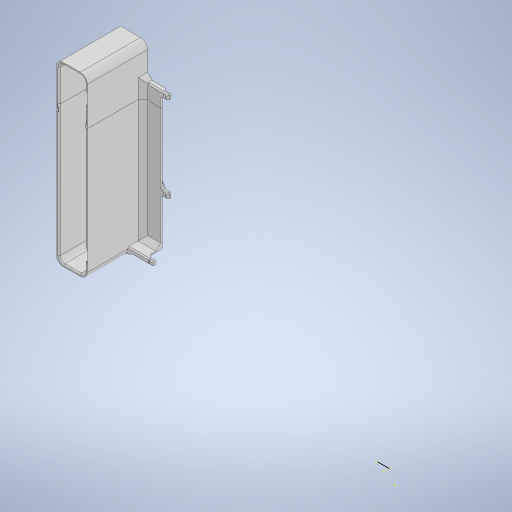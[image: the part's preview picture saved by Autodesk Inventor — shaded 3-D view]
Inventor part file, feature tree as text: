
AUTODESK INVENTOR PART (.ipt)
format: ipt  version: 2024.1 (Build 281209000, 209)  size: 7,091,200 bytes
history: native  units: mm
features: projected_geometry x112, sketch x91, extrude x86, chamfer x77, other x33, plane x15, fillet x9, pattern_linear x7, mirror x3, loft x2, pattern_circular x1, sweep x1
ambient origin geometry x8: Origin, YZ Plane, XZ Plane, XY Plane, X Axis, Y Axis, Z Axis, Center Point
bodies: Solid3 (feature_tree), Solid4 (feature_tree), Solid8 (feature_tree), Solid9 (feature_tree), Solid14 (feature_tree), Solid16 (feature_tree), Solid26 (feature_tree), Solid27 (feature_tree)
feature tree (437):
  other  "synth-a"
  other  "Blocks"
  extrude  "Extrusion1"  Depth=30.22mm
  plane  "Work Plane1"
  extrude  "Extrusion2"  Depth=17.13mm
  plane  "Work Plane2"
  mirror  "Mirror1"
  sketch  "Sketch3"  dims[d5=2.61mm d6=226.0mm]
  extrude  "Extrusion3"  Depth=226.0mm
  extrude  "Extrusion4"  Depth=8.2mm
  extrude  "Extrusion5"  Depth=35.4mm
  fillet  "Fillet1"  Radius=7.89mm
  pattern_linear  "Rectangular Pattern1"  Count1=56 Spacing1=0.0mm
  extrude  "Extrusion6"  Depth=3.14mm
  chamfer  "Chamfer1"  Distance=13.85mm
  chamfer  "Chamfer2"  Distance=440.5mm
  chamfer  "Chamfer3"  Distance=11.2mm
  chamfer  "Chamfer4"  Distance=3.1mm
  chamfer  "Chamfer5"  Distance=220.0mm
  chamfer  "Chamfer6"  Distance=7.26mm
  chamfer  "Chamfer7"  Distance=7.0mm Angle=45.0deg
  chamfer  "Chamfer8"  Distance=7.0mm Angle=45.0deg
  chamfer  "Chamfer9"  Distance=7.0mm Angle=45.0deg
  chamfer  "Chamfer10"  Distance=7.0mm Angle=45.0deg
  chamfer  "Chamfer11"  Distance=7.0mm Angle=45.0deg
  chamfer  "Chamfer12"  Distance=7.0mm Angle=45.0deg
  chamfer  "Chamfer13"  Distance=7.0mm Angle=45.0deg
  chamfer  "Chamfer14"  Distance=7.0mm Angle=45.0deg
  chamfer  "Chamfer15"  Distance=7.0mm Angle=45.0deg
  fillet  "Fillet2"  Radius=1.5mm
  pattern_linear  "Rectangular Pattern2"  Count1=3  [1 undecoded]
  extrude  "Extrusion7"  Depth=40.0mm
  extrude  "Extrusion8"  Depth=40.0mm
  plane  "Work Plane3"
  extrude  "Extrusion9"  Depth=20.42mm TaperAngle=0.0deg
  plane  "Work Plane7"
  plane  "Work Plane9"
  extrude  "Extrusion18"  Depth=60.6mm
  sketch  "Sketch26"  dims[d46=3.63mm]
  extrude  "Extrusion24"  Depth=35.8mm
  extrude  "Extrusion25"  Depth=2.9mm TaperAngle=0.0deg
  fillet  "Fillet3"  [1 undecoded]
  extrude  "Extrusion10"  Depth=90.0mm
  sketch  "Sketch12"  dims[d25=18.04mm]
  plane  "Work Plane5"
  extrude  "Extrusion12"  Depth=10.0mm
  extrude  "Extrusion14"  Depth=5.0mm
  extrude  "Extrusion15"  Depth=5.0mm
  plane  "Work Plane6"
  extrude  "Extrusion16"  Depth=16.580628mm
  mirror  "Mirror2"
  extrude  "Extrusion77"  Depth=20.0mm
  extrude  "Extrusion78"  Depth=5.0mm
  extrude  "Extrusion79"  Depth=2.0mm
  extrude  "Extrusion80"  Depth=2.5mm
  extrude  "Extrusion81"  Depth=2.5mm
  extrude  "Extrusion82"  Depth=2.5mm
  pattern_linear  "Rectangular Pattern4"  Count1=3 Spacing1=241.0mm
  chamfer  "Chamfer64"  Distance=10.0mm
  chamfer  "Chamfer65"  Distance=0.01mm
  chamfer  "Chamfer66"  Distance=10.0mm
  pattern_linear  "Rectangular Pattern3"  Count1=2 Spacing1=105.0mm
  pattern_linear  "Rectangular Pattern10"  Count1=2 Spacing1=0.0mm
  extrude  "Extrusion17"  Depth=2.0mm
  extrude  "Extrusion56"  Depth=4.0mm
  extrude  "Extrusion57"  Depth=3.0mm
  plane  "Work Plane8"
  plane  "Work Plane11"
  extrude  "Extrusion33"  Depth=4.0mm
  fillet  "Fillet6"  Radius=1.0mm
  extrude  "Extrusion29"  Depth=2.0mm
  extrude  "Extrusion31"  Depth=10.0mm
  extrude  "Extrusion32"  Depth=292.1mm
  extrude  "Extrusion34"  Depth=8.0mm
  extrude  "Extrusion35"  Depth=0.5mm TaperAngle=0.0deg
  extrude  "Extrusion36"  Depth=28.3mm
  fillet  "Fillet7"  Radius=28.3mm
  pattern_circular  "Circular Pattern1"  Count=7  [1 undecoded]
  extrude  "Extrusion37"  Depth=11.3mm
  plane  "Work Plane17"
  extrude  "Extrusion38"  Depth=13.54mm
  extrude  "Extrusion39"  Depth=2.0mm
  extrude  "Extrusion40"  Depth=2.0mm
  extrude  "Extrusion41"  Depth=2.0mm
  extrude  "Extrusion43"  Depth=2.0mm
  extrude  "Extrusion44"  Depth=2.0mm
  sketch  "Sketch47"  dims[d121=20.0mm d122=0.0mm d123=5.0mm]
  chamfer  "Chamfer18"  Distance=15.4mm
  chamfer  "Chamfer19"  Distance=2.0mm Angle=45.0deg
  chamfer  "Chamfer20"  Distance=2.0mm
  extrude  "Extrusion45"  Depth=2.0mm
  chamfer  "Chamfer21"  Distance=13.0mm
  extrude  "Extrusion46"  Depth=2.0mm
  extrude  "Extrusion49"  Depth=2.0mm TaperAngle=0.0deg
  extrude  "Extrusion50"  Depth=2.0mm
  plane  "Work Plane13"
  extrude  "Extrusion51"  Depth=2.0mm TaperAngle=0.0deg
  pattern_linear  "Rectangular Pattern7"  Spacing1=10.0mm  [1 undecoded]
  extrude  "Extrusion52"  Depth=4.0mm
  extrude  "Extrusion53"  Depth=2.0mm TaperAngle=0.0deg
  extrude  "Extrusion54"  Depth=2.0mm
  extrude  "Extrusion55"  Depth=2.0mm TaperAngle=0.0deg
  chamfer  "Chamfer22"  Distance=2.0mm Angle=45.0deg
  chamfer  "Chamfer23"  Distance=2.0mm
  chamfer  "Chamfer24"  Distance=150.0mm
  chamfer  "Chamfer25"  Distance=0.02mm
  extrude  "Extrusion74"  Depth=2.0mm TaperAngle=0.0deg
  chamfer  "Chamfer58"  Distance=14.55mm
  chamfer  "Chamfer59"  Distance=7.0mm
  plane  "Work Plane16"
  extrude  "Extrusion73"  Depth=2.0mm
  plane  "Work Plane14"
  extrude  "Extrusion75"  Depth=2.0mm
  chamfer  "Chamfer60"  Distance=2.5mm
  plane  "Work Plane15"
  extrude  "Extrusion71"  Depth=2.0mm
  extrude  "Extrusion72"  Depth=2.0mm TaperAngle=0.0deg
  chamfer  "Chamfer61"  Distance=17.0mm
  chamfer  "Chamfer62"  Distance=7.0mm
  extrude  "Extrusion83"  Depth=2.0mm
  extrude  "Extrusion84"  Depth=241.0mm
  extrude  "Extrusion85"  Depth=2.0mm
  extrude  "Extrusion86"  Depth=2.0mm
  extrude  "Extrusion87"  TaperAngle=90.0deg  [1 undecoded]
  loft  "Loft2"
  chamfer  "Chamfer68"  Angle=90.0deg  [1 undecoded]
  chamfer  "Chamfer69"  Distance=420.0mm
  chamfer  "Chamfer70"  Distance=7.0mm
  chamfer  "Chamfer71"  Distance=40.0mm
  chamfer  "Chamfer72"  Distance=7.0mm
  chamfer  "Chamfer73"  Distance=10.0mm
  chamfer  "Chamfer79"  Distance=4.2mm
  chamfer  "Chamfer80"  [1 undecoded]
  chamfer  "Chamfer81"  Distance=2.5mm
  chamfer  "Chamfer82"  Distance=8.0mm
  chamfer  "Chamfer83"  Distance=10.0mm
  sketch  "Sketch109"  dims[d216=16.2mm d217=28.3mm d218=28.3mm]
  extrude  "Extrusion91"  Depth=2.0mm TaperAngle=0.0deg
  chamfer  "Chamfer84"  Distance=1.0mm
  chamfer  "Chamfer85"  Distance=1.0mm
  chamfer  "Chamfer86"  Distance=160.0mm Angle=360.0deg
  chamfer  "Chamfer87"  Distance=13.0mm
  pattern_linear  "Rectangular Pattern9"  Spacing1=1.5mm  [1 undecoded]
  extrude  "Extrusion58"  Depth=2.0mm TaperAngle=0.0deg
  extrude  "Extrusion59"  Depth=2.0mm TaperAngle=0.0deg
  chamfer  "Chamfer26"  Distance=3.5mm
  chamfer  "Chamfer27"  Distance=7.1mm
  chamfer  "Chamfer28"  Distance=2.0mm
  chamfer  "Chamfer29"  Distance=8.8mm
  chamfer  "Chamfer30"  Distance=48.0mm
  chamfer  "Chamfer31"  Distance=30.0mm
  chamfer  "Chamfer32"  Distance=40.0mm
  extrude  "Extrusion60"  Depth=2.0mm
  extrude  "Extrusion61"  Depth=2.0mm
  loft  "Loft1"
  extrude  "Extrusion62"  Depth=2.0mm
  sweep  "Sweep1"
  chamfer  "Chamfer33"  Distance=12.0mm
  chamfer  "Chamfer35"  Distance=11.5mm
  chamfer  "Chamfer36"  Distance=8.0mm
  extrude  "audio-io-device"  Depth=4.0mm
  fillet  "Fillet4"  Radius=2.0mm
  extrude  "Extrusion20"  Depth=3.0mm
  extrude  "Extrusion21"  Depth=10.0mm TaperAngle=0.0deg
  extrude  "Extrusion22"  Depth=10.0mm TaperAngle=0.0deg
  chamfer  "Chamfer16"  Distance=2.0mm Angle=45.0deg
  fillet  "Fillet5"  Radius=2.0mm
  extrude  "Extrusion23"  Depth=4.0mm TaperAngle=45.0deg
  extrude  "Extrusion92"  Depth=2.0mm
  fillet  "Fillet8"  Radius=23.0mm
  extrude  "Extrusion26"  Depth=10.0mm TaperAngle=0.0deg
  extrude  "Extrusion27"  Depth=2.0mm
  chamfer  "Chamfer17"  Distance=2.0mm Angle=45.0deg
  plane  "Work Plane10"
  mirror  "Mirror3"
  extrude  "Extrusion28"  Depth=2.0mm
  extrude  "io-device-clip"  Depth=10.0mm
  extrude  "Extrusion93"  Depth=10.0mm TaperAngle=0.0deg
  fillet  "Fillet9"  Radius=20.0mm
  extrude  "Extrusion64"  Depth=2.0mm
  extrude  "Extrusion65"  Depth=2.0mm
  extrude  "Extrusion66"  Depth=1.0mm
  extrude  "Extrusion67"  Depth=1.0mm
  chamfer  "Chamfer38"  Distance=5.75mm
  extrude  "Extrusion69"  Depth=3.0mm
  extrude  "Extrusion70"  Depth=2.0mm
  chamfer  "Chamfer48"  Distance=6.5mm
  chamfer  "Chamfer49"  Angle=90.0deg  [1 undecoded]
  chamfer  "Chamfer50"  Distance=1.5mm
  chamfer  "Chamfer51"  Distance=1.5mm
  chamfer  "Chamfer52"  Distance=1.5mm
  chamfer  "Chamfer53"  Distance=1.5mm
  chamfer  "Chamfer54"  Distance=1.5mm
  chamfer  "Chamfer55"  Distance=1.5mm
  chamfer  "Chamfer56"  Distance=9.0mm
  chamfer  "Chamfer57"  Distance=4.0mm
  chamfer  "Chamfer74"  Distance=9.0mm
  chamfer  "Chamfer75"  Distance=10.0mm
  chamfer  "Chamfer76"  Distance=20.0mm
  chamfer  "Chamfer77"  Distance=0.02mm
  chamfer  "Chamfer78"  Distance=0.02mm
  extrude  "Extrusion88"  Depth=9.0mm TaperAngle=0.0deg
  extrude  "Extrusion89"  Depth=2.0mm TaperAngle=0.0deg
  extrude  "Extrusion94"  Depth=2.0mm
  extrude  "Extrusion95"  Depth=2.0mm
  chamfer  "Chamfer88"  Distance=9.0mm
  chamfer  "Chamfer89"  Distance=4.5mm
  chamfer  "Chamfer90"  Distance=48.0mm
  sketch  "Sketch1"  dims[d0=205.0mm d1=30.22mm]
  sketch  "Sketch2"  dims[d2=102.5mm d3=17.13mm]
  projected_geometry  "Projected Loop1"
  sketch  "Sketch4"  dims[d7=12.4mm d8=8.2mm]
  projected_geometry  "Projected Loop2"
  sketch  "Sketch5"  dims[d9=4.5mm d10=35.4mm d11=7.89mm]
  sketch  "Sketch6"  dims[d12=9.657689mm]
  projected_geometry  "Projected Loop3"
  sketch  "Sketch7"  dims[d13=17.466067mm d14=560.0mm d15=0.0mm]
  sketch  "Sketch8"  dims[d16=-18.52mm d17=3.14mm d18=13.85mm d19=0.0mm]
  sketch  "Sketch9"  dims[d20=17.38mm]
  sketch  "Sketch10"  dims[d21=91.58mm d22=440.5mm d23=0.0mm]
  projected_geometry  "Projected Loop4"
  projected_geometry  "Projected Loop5"
  projected_geometry  "Projected Loop6"
  other  "stand-leg-A"
  other  "Pattern of stand-leg-A:1"
  other  "Pattern of stand-leg-A:2"
  sketch  "Sketch11"  dims[d24=2.4mm]
  sketch  "Sketch14"  dims[d26=18.56mm d27=11.2mm d28=0.0mm]
  projected_geometry  "Projected Loop8"
  sketch  "Sketch15"  dims[d29=81.62mm d30=3.1mm d31=0.0mm]
  sketch  "Sketch17"  dims[d32=1.5mm d33=220.0mm d35=20.0mm]
  projected_geometry  "Projected Loop10"
  projected_geometry  "Projected Loop11"
  projected_geometry  "Projected Loop12"
  projected_geometry  "Projected Loop13"
  sketch  "Sketch18"  dims[d36=48.6mm]
  sketch  "Sketch19"  dims[d37=8.7mm]
  projected_geometry  "Projected Loop14"
  projected_geometry  "Projected Loop15"
  projected_geometry  "Projected Loop16"
  projected_geometry  "Projected Loop17"
  projected_geometry  "Projected Loop18"
  projected_geometry  "Projected Loop19"
  projected_geometry  "Projected Loop20"
  projected_geometry  "Projected Loop21"
  other  "crossbars"
  sketch  "Sketch20"  dims[d38=8.7mm]
  sketch  "Sketch21"  dims[d39=8.7mm]
  other  "audio-io"
  sketch  "Sketch22"  dims[d40=8.7mm]
  projected_geometry  "Projected Loop22"
  sketch  "Sketch23"  dims[d41=8.7mm]
  sketch  "Sketch24"  dims[d44=3.63mm]
  sketch  "Sketch25"  dims[d45=3.63mm]
  projected_geometry  "Projected Loop23"
  sketch  "Sketch27"  dims[d47=3.63mm]
  projected_geometry  "Projected Loop24"
  other  "audio-io-stand"
  sketch  "Sketch28"  dims[d48=3.63mm]
  projected_geometry  "Projected Loop25"
  sketch  "Sketch29"  dims[d49=3.63mm d50=7.26mm d51=0.0mm d52=5.0mm d53=7.0mm d54=45.0deg d55=5.0mm d56=7.0mm d57=45.0deg d58=5.0mm d59=7.0mm d60=45.0deg d61=5.0mm d62=7.0mm d63=45.0deg d64=5.0mm d65=7.0mm d66=45.0deg d67=1.5mm d68=7.0mm d69=45.0deg d70=1.5mm d71=7.0mm d72=45.0deg d73=1.5mm d74=7.0mm d75=45.0deg d76=1.5mm d77=7.0mm d78=45.0deg]
  sketch  "Sketch30"  dims[d79=1.5mm d80=7.0mm d81=45.0deg]
  projected_geometry  "Projected Loop26"
  sketch  "Sketch34"  dims[d82=1.5mm d83=7.0mm d84=45.0deg]
  projected_geometry  "Projected Loop29"
  sketch  "Sketch35"  dims[d85=1.5mm d86=7.0mm d87=45.0deg]
  other  "back-uprights"
  projected_geometry  "Projected Loop30"
  sketch  "Sketch36"  dims[d88=1.5mm d89=7.0mm d90=45.0deg]
  other  "looper"
  sketch  "Sketch37"  dims[d91=1.5mm d92=7.0mm d93=45.0deg]
  sketch  "Sketch38"  dims[d94=1.5mm d95=7.0mm d96=45.0deg d97=1.5mm d98=30.0mm d100=140.0mm]
  sketch  "Sketch39"  dims[d101=17.93mm d102=40.0mm]
  sketch  "Sketch40"  dims[d103=40.0mm d104=40.0mm]
  sketch  "Sketch41"  dims[d105=35.4mm d106=20.42mm d107=0.0mm]
  projected_geometry  "Projected Loop31"
  projected_geometry  "Projected Loop32"
  other  "top-arm"
  sketch  "Sketch42"  dims[d108=20.16mm d109=60.6mm]
  projected_geometry  "Projected Loop33"
  sketch  "Sketch43"  dims[d110=60.6mm d111=35.8mm]
  projected_geometry  "Projected Loop34"
  sketch  "Sketch44"  dims[d112=52.9mm d113=2.9mm d114=0.0mm d115=-10.0mm]
  sketch  "Sketch45"  dims[d116=20.0mm d118=90.0mm]
  projected_geometry  "Projected Loop35"
  sketch  "Sketch46"  dims[d119=10.0mm d120=20.0mm]
  projected_geometry  "Projected Loop36"
  projected_geometry  "Projected Loop37"
  sketch  "Sketch48"  dims[d124=5.0mm d125=5.0mm]
  projected_geometry  "Projected Loop38"
  sketch  "Sketch50"  dims[d126=30.0mm d127=16.580628mm]
  projected_geometry  "Projected Loop40"
  other  "Pattern of back-uprights:3"
  other  "Pattern of back-uprights:4"
  sketch  "Sketch57"  dims[d128=8.0mm d129=20.0mm]
  projected_geometry  "Projected Loop42"
  projected_geometry  "Projected Loop43"
  sketch  "Sketch58"  dims[d133=5.0mm d134=5.0mm]
  projected_geometry  "Projected Loop44"
  sketch  "Sketch59"  dims[d135=18.0mm d136=2.0mm]
  projected_geometry  "Projected Loop45"
  projected_geometry  "Projected Loop46"
  projected_geometry  "Projected Loop47"
  sketch  "Sketch60"  dims[d139=120.0mm d140=2.5mm]
  projected_geometry  "Projected Loop48"
  projected_geometry  "Projected Loop49"
  other  "back-crossbeam"
  sketch  "Sketch61"  dims[d141=2.5mm d142=2.5mm]
  projected_geometry  "Projected Loop50"
  sketch  "Sketch62"  dims[d143=2.5mm d144=2.5mm]
  other  "sqr-connector"
  other  "sqr-connector_1"
  other  "sqr-connector_2"
  sketch  "Sketch63"  dims[d145=2.5mm]
  projected_geometry  "Projected Loop51"
  projected_geometry  "Projected Loop52"
  projected_geometry  "Projected Loop53"
  sketch  "Sketch66"  dims[d146=95.0mm]
  projected_geometry  "Projected Loop55"
  sketch  "Sketch67"  dims[d147=2.5mm d148=30.0mm d150=241.0mm]
  projected_geometry  "Projected Loop56"
  projected_geometry  "Projected Loop57"
  projected_geometry  "Projected Loop58"
  projected_geometry  "Projected Loop59"
  projected_geometry  "Projected Loop60"
  projected_geometry  "Projected Loop61"
  projected_geometry  "Projected Loop62"
  projected_geometry  "Projected Loop63"
  projected_geometry  "Projected Loop64"
  projected_geometry  "Projected Loop65"
  sketch  "Sketch68"  dims[d151=2.0mm]
  projected_geometry  "Projected Loop66"
  projected_geometry  "Projected Loop67"
  sketch  "Sketch69"  dims[d152=10.0mm]
  projected_geometry  "Projected Loop68"
  projected_geometry  "Projected Loop69"
  other  "TOP-CROSSBEAM"
  sketch  "Sketch70"  dims[d153=7.0mm]
  projected_geometry  "Projected Loop70"
  other  "angled-member"
  sketch  "Sketch71"  dims[d154=10.0mm]
  projected_geometry  "Projected Loop71"
  other  "Edges1"
  other  "Edges2"
  sketch  "Sketch74"  dims[d155=6.5mm]
  projected_geometry  "Projected Loop74"
  sketch  "Sketch75"  dims[d156=6.5mm]
  projected_geometry  "Projected Loop75"
  sketch  "Sketch76"  dims[d158=0.01mm]
  sketch  "Sketch77"  dims[d159=5.0mm]
  projected_geometry  "Projected Loop76"
  sketch  "Sketch78"  dims[d161=8.0mm]
  projected_geometry  "Projected Loop77"
  sketch  "Sketch79"  dims[d162=0.01mm]
  projected_geometry  "Projected Loop78"
  sketch  "Sketch80"  dims[d163=15.0mm]
  projected_geometry  "Projected Loop79"
  projected_geometry  "Projected Loop80"
  projected_geometry  "Projected Loop81"
  sketch  "Sketch81"  dims[d164=2.0mm d165=10.0mm d166=0.0mm d169=0.01mm d170=0.0mm]
  projected_geometry  "Projected Loop82"
  sketch  "Sketch83"  dims[d171=0.01mm d174=10.0mm d175=0.0mm]
  sketch  "Sketch85"  dims[d176=0.01mm d177=0.0mm]
  projected_geometry  "Projected Loop83"
  projected_geometry  "Projected Loop84"
  projected_geometry  "Projected Loop85"
  sketch  "Sketch86"  dims[d178=8.0mm]
  sketch  "Sketch88"  dims[d179=7.0mm]
  sketch  "Sketch89"  dims[d180=-8.0mm]
  projected_geometry  "Projected Loop87"
  sketch  "Sketch90"  dims[d181=6.0mm]
  projected_geometry  "Projected Loop88"
  sketch  "Sketch91"  dims[d182=4.0mm]
  sketch  "Sketch94"  dims[d183=3.0mm]
  sketch  "Sketch95"  dims[d184=3.0mm]
  sketch  "Sketch96"  dims[d185=2.0mm]
  projected_geometry  "Projected Loop90"
  projected_geometry  "Projected Loop91"
  sketch  "Sketch97"  dims[d186=7.0mm d187=0.0mm d188=20.0mm d190=105.0mm d191=20.0mm d192=0.0mm]
  projected_geometry  "Projected Loop92"
  projected_geometry  "Projected Loop93"
  projected_geometry  "Projected Loop94"
  projected_geometry  "Projected Loop95"
  other  "feet"
  sketch  "Sketch98"  dims[d193=2.5mm d194=2.0mm]
  projected_geometry  "Projected Loop96"
  projected_geometry  "Projected Loop97"
  other  "rubber-top-base"
  sketch  "Sketch99"  dims[d195=90.0deg d196=4.0mm d197=7.0mm]
  projected_geometry  "Projected Loop98"
  other  "rubber-stopper"
  other  "Pattern of feet:7"
  other  "Pattern of feet:8"
  sketch  "Sketch100"  dims[d198=4.5mm d199=3.0mm]
  projected_geometry  "Projected Loop99"
  projected_geometry  "Projected Loop100"
  projected_geometry  "Projected Loop101"
  projected_geometry  "Projected Loop102"
  other  "rubber-toppers-top"
  sketch  "Sketch101"  dims[d200=4.0mm d201=4.0mm d202=1.0mm]
  projected_geometry  "Projected Loop103"
  other  "rubber-cap"
  sketch  "Sketch102"  dims[d203=7.0mm d204=2.0mm]
  projected_geometry  "Projected Loop104"
  other  "rubber-tip"
  sketch  "Sketch103"  dims[d205=13.0mm d206=0.0mm d207=10.0mm]
  projected_geometry  "Projected Loop105"
  sketch  "Sketch104"  dims[d208=107.0mm d209=292.1mm]
  projected_geometry  "Projected Loop106"
  other  "Edges3"
  other  "Edges4"
  sketch  "Sketch105"  dims[d210=43.8mm d211=0.0mm d212=8.0mm]
  projected_geometry  "Projected Loop107"
  sketch  "Sketch106"  dims[d213=1.59mm d214=0.5mm d215=0.0mm]
  projected_geometry  "Projected Loop108"
  projected_geometry  "Projected Loop110"
  sketch  "Sketch110"  dims[d219=28.3mm]
  projected_geometry  "Projected Loop111"
  sketch  "Sketch111"  dims[d220=23.9mm d221=70.0mm d222=0.0mm]
  projected_geometry  "Projected Loop112"
  projected_geometry  "Projected Loop113"
  sketch  "Sketch112"  dims[d223=11.7mm d224=11.3mm]
  projected_geometry  "Projected Loop114"
  projected_geometry  "Projected Loop115"
  projected_geometry  "Projected Loop116"
  projected_geometry  "Projected Loop117"
  projected_geometry  "Projected Loop118"
  sketch  "Sketch113"  dims[d225=13.54mm d226=13.54mm]
  projected_geometry  "Projected Loop119"
  sketch  "Sketch114"  dims[d227=22.0mm d228=60.0mm d229=30.0mm d230=30.0mm d231=30.0mm d232=13.0mm d233=15.4mm d234=0.0mm d235=5.0mm d236=2.0mm d237=45.0deg d238=2.0mm d239=13.0mm d240=13.0mm d241=26.0mm d242=42.0mm d243=0.0mm d244=11.0mm d245=42.0mm d246=0.0mm d247=10.0mm d248=0.0mm d255=4.0mm d256=100.0mm d257=0.0mm d258=5.0mm d259=2.0mm d260=0.0mm d261=2.0mm d262=2.0mm d263=45.0deg d269=2.0mm d270=0.0mm d271=150.0mm d272=0.02mm d273=15.0mm d274=0.0mm d279=14.55mm d280=0.0mm d282=7.0mm d283=5.0mm d285=5.0mm d287=2.5mm d288=2.5mm d289=14.55mm d290=0.0mm d292=17.0mm d293=7.0mm d294=10.5mm d295=30.0mm d297=241.0mm d298=100.0mm d300=32.16mm d301=90.0deg d302=54.4mm d303=90.0deg d304=420.0mm d305=0.0mm d306=7.0mm d307=40.0mm d308=7.0mm d309=10.0mm d310=0.0mm d311=4.2mm d312=0.0mm d313=0.0mm d314=2.5mm d315=8.0mm d316=10.0mm d317=1.5mm d318=0.0mm d319=1.0mm d320=1.0mm d321=160.0mm d322=360.0deg d324=13.0mm d325=1.5mm d326=0.0mm d327=1.2mm d328=0.0mm d329=2.5mm d330=0.0mm d331=3.5mm d332=0.0mm d333=7.1mm d334=2.0mm d335=0.0mm d337=8.8mm d338=48.0mm d339=30.0mm d340=40.0mm d341=43.0mm d342=135.0mm d343=36.0mm d344=22.0mm d345=146.0mm d346=12.0mm d347=11.5mm d348=8.0mm d349=4.0mm d350=2.0mm d351=3.0mm d354=10.0mm d355=0.0mm d356=10.0mm d357=0.0mm d360=8.0mm d361=2.0mm d362=45.0deg d363=5.0mm d364=2.0mm d365=45.0deg d366=4.0mm d367=2.0mm d368=45.0deg d370=36.0mm d371=23.0mm d372=10.0mm d373=0.0mm d374=20.0mm d376=8.0mm d377=2.0mm d378=45.0deg d379=2.5mm d380=10.0mm d381=10.0mm d382=0.0mm d422=20.0mm d423=1.5mm d424=1.5mm d425=1.0mm d426=1.0mm d427=5.75mm d428=3.0mm d430=6.5mm d431=6.5mm d432=90.0deg d433=1.5mm d434=1.5mm d435=1.5mm d436=1.5mm d437=1.5mm d438=1.5mm d439=9.0mm d440=0.0mm d441=4.0mm d442=9.0mm d443=0.0mm d444=10.0mm d445=0.0mm d446=20.0mm d447=0.02mm d448=0.02mm d449=9.0mm d450=0.0mm d451=15.0mm d452=0.0mm d453=20.0mm d454=1.5mm d455=1.5mm d456=1.0mm d457=1.0mm d458=5.75mm d459=3.0mm d460=6.5mm d461=6.5mm d462=90.0deg d463=1.5mm d464=1.5mm d465=1.5mm d466=1.5mm d467=1.5mm d468=1.5mm d485=20.0mm d486=1.5mm d487=1.5mm d488=1.0mm d489=1.0mm d490=5.75mm d491=3.0mm d492=6.5mm d493=6.5mm d494=90.0deg d495=1.5mm d496=1.5mm d497=1.5mm d498=1.5mm d499=1.5mm d500=1.5mm d501=20.0mm d502=1.5mm d503=1.5mm d504=1.0mm d505=1.0mm d506=5.75mm d507=3.0mm d508=6.5mm d509=6.5mm d510=90.0deg d511=1.5mm d512=1.5mm d513=1.5mm d514=1.5mm d515=1.5mm d516=1.5mm d517=22.0mm d518=120.0mm d519=9.0mm d520=0.0mm d521=4.5mm d522=48.0mm d523=9.0mm d524=0.0mm d525=2.5mm d526=2.5mm d527=2.0mm d528=2.0mm d529=6.0mm d530=4.5mm d531=30.0deg d532=3.3mm d533=10.0mm d534=2.0mm d535=45.0deg d536=7.0mm d537=2.0mm d538=45.0deg d539=3.0mm d540=2.0mm d541=45.0deg d542=3.0mm d543=2.0mm d544=45.0deg d545=0.02mm d546=0.02mm d547=10.0mm d548=0.0mm d549=8.0mm d550=8.0mm d552=20.0mm d553=20.0mm d554=8.0mm d555=8.0mm d556=20.0mm d558=20.0mm d559=0.0mm d560=0.0mm d561=10.0mm d562=0.0mm d563=5.0mm d564=0.0mm d565=2.0mm d566=2.0mm d567=45.0deg d568=1.0mm d569=2.0mm d570=45.0deg d571=2.0mm d572=2.0mm d573=45.0deg d574=1.0mm d575=2.0mm d576=45.0deg d577=4.0mm d578=2.0mm d579=45.0deg d580=2.0mm d581=2.0mm d582=45.0deg d583=4.0mm d584=2.0mm d585=45.0deg d586=0.02mm d587=8.0mm d588=15.0mm d589=0.0mm d590=0.02mm d591=8.0mm d592=9.8mm d593=0.0mm d594=0.0mm d595=90.0deg d596=0.0mm d597=90.0deg d598=9.8mm d599=0.0mm d600=0.0mm d601=0.0mm d602=2.0mm d603=2.0mm d604=45.0deg d608=2.0mm d609=2.0mm d610=45.0deg d611=3.0mm d612=2.0mm d613=45.0deg d614=0.02mm d615=9.0mm d616=0.0mm d617=9.0mm d618=0.0mm d619=0.02mm d620=7.0mm d621=0.0mm d622=49.5mm d623=0.0mm d624=1.0mm d625=0.0mm d634=6.5mm d635=2.0mm d636=45.0deg d643=30.0mm d644=30.0mm d645=0.0mm d667=0.0mm d668=60.0mm d669=19.35mm d670=7.75mm d671=0.0mm d672=0.0mm d673=8.0mm d674=2.0mm d675=45.0deg d676=8.0mm d677=2.0mm d678=45.0deg d679=2.0mm d680=2.0mm d681=45.0deg d682=2.0mm d683=2.0mm d684=45.0deg d685=2.0mm d686=2.0mm d687=45.0deg d688=2.0mm d689=2.0mm d690=45.0deg d691=2.0mm d692=2.0mm d693=45.0deg d694=2.0mm d695=2.0mm d696=45.0deg d697=8.0mm d698=2.0mm d699=45.0deg d700=8.0mm d701=2.0mm d702=45.0deg d713=2.0mm d714=0.0mm d719=4.0mm d720=4.0mm d721=2.0mm d722=0.0mm d728=2.0mm d729=0.0mm d730=0.0mm d731=0.0mm d732=4.0mm d733=2.0mm d734=45.0deg d735=3.0mm d736=2.0mm d737=45.0deg d738=27.925268mm d739=27.925268mm d743=2.0mm d744=0.0mm d747=1.0mm d748=1.0mm d749=1.89128mm d750=1.89128mm d751=1.5mm d754=1.79mm d755=2.0mm d756=45.0deg d757=4.0mm d758=2.0mm d759=4.0mm d760=4.0mm d761=4.0mm d762=4.0mm d763=4.0mm d764=4.0mm d765=3.0mm d766=3.0mm d767=3.0mm d768=2.0mm d769=20.0mm d771=241.0mm d772=2.0mm d773=2.0mm d774=45.0deg d775=2.0mm d776=2.0mm d777=45.0deg d781=7.0mm d782=4.0mm d783=3.0mm d784=3.0mm d785=18.0mm d786=16.0mm d787=2.0mm d788=0.0mm d789=1.5mm d790=1.5mm d791=2.0mm d792=0.0mm d793=6.0mm d795=3.0mm d796=20.0mm d798=20.0mm d799=2.0mm d800=20.0mm d801=2.0mm d802=0.0mm d803=20.0mm d804=0.3mm d805=0.3mm d806=0.3mm d807=0.3mm d808=2.0mm d809=2.0mm d810=2.0mm d811=2.0mm d812=2.0mm d813=2.0mm d814=2.0mm d815=2.0mm d816=2.0mm d817=2.0mm d818=2.0mm d819=2.0mm d820=2.0mm d821=2.0mm d822=2.0mm d823=2.0mm d824=2.0mm d825=2.0mm d826=2.0mm d827=2.0mm d828=2.0mm d829=2.0mm d830=2.0mm d831=2.0mm d832=2.0mm d833=2.0mm d834=2.0mm d835=2.0mm d836=2.0mm d837=2.0mm d838=2.0mm d839=2.0mm d840=4.0mm d841=0.0mm d842=0.3mm d843=0.3mm d844=2.0mm d845=2.0mm d846=2.0mm d847=2.0mm d848=2.0mm d849=2.0mm d850=2.0mm d851=2.0mm d852=2.0mm d853=2.0mm d854=2.0mm d855=2.0mm d856=2.0mm d857=2.0mm d858=2.0mm d859=2.0mm d860=3.0mm d861=0.0mm d862=0.3mm d863=2.0mm d864=2.0mm d865=2.0mm d866=2.0mm d867=2.0mm d868=2.0mm d869=2.0mm d870=2.0mm d871=3.0mm d872=0.0mm d873=30.0mm d875=241.0mm d876=0.3mm d877=0.3mm d878=0.3mm d879=0.3mm d880=2.0mm d881=2.0mm d882=2.0mm d883=2.0mm d884=2.0mm d885=2.0mm d886=2.0mm d887=2.0mm d888=2.0mm d889=2.0mm d890=2.0mm d891=2.0mm d892=2.0mm d893=2.0mm d894=2.0mm d895=2.0mm d896=2.0mm d897=2.0mm d898=2.0mm d899=2.0mm d900=2.0mm d901=2.0mm d902=2.0mm d903=2.0mm d904=2.0mm d905=2.0mm d906=2.0mm d907=2.0mm d908=2.0mm d909=2.0mm d910=2.0mm d911=2.0mm d912=3.0mm d913=0.0mm d914=1.0mm d915=2.0mm d916=45.0deg d917=1.0mm d918=2.0mm d919=45.0deg d920=1.0mm d921=2.0mm d922=45.0deg d923=0.3mm d924=2.0mm d925=2.0mm d926=2.0mm d927=2.0mm d928=2.0mm d929=2.0mm d930=2.0mm d931=2.0mm d932=3.0mm d933=0.0mm d934=0.3mm d935=3.0mm d936=0.0mm d937=0.3mm d938=3.0mm d939=0.0mm d940=0.25mm d941=0.0mm d942=0.0mm d943=90.0deg d944=0.0mm d945=90.0deg d949=1.0mm d950=2.0mm d951=45.0deg d952=1.0mm d953=2.0mm d954=45.0deg d955=1.0mm d956=2.0mm d957=45.0deg d958=1.0mm d959=2.0mm d960=45.0deg d961=1.0mm d962=2.0mm d963=45.0deg d964=1.0mm d965=2.0mm d966=45.0deg d967=1.0mm d968=2.0mm d969=45.0deg d970=1.5mm d971=2.0mm d972=45.0deg d973=1.5mm d974=2.0mm d975=45.0deg d976=1.5mm d977=2.0mm d978=45.0deg d979=5.0mm d980=2.0mm d981=45.0deg d982=0.25mm d983=0.0mm d984=10.0mm d985=0.0mm d1008=1.5mm d1009=7.0mm d1010=2.0mm d1011=45.0deg d1012=8.0mm d1013=2.0mm d1014=45.0deg d1015=5.0mm d1016=2.0mm d1017=45.0deg d1018=2.2mm d1019=2.0mm d1020=45.0deg d1021=4.0mm d1022=2.0mm d1023=45.0deg d1024=14.0mm d1025=6.0mm d1026=0.0mm d1027=0.0mm d1028=4.0mm d1029=2.0mm d1030=45.0deg d1031=3.0mm d1032=2.0mm d1033=45.0deg d1034=4.0mm d1035=2.0mm d1036=45.0deg d1037=4.0mm d1038=2.0mm d1039=45.0deg d1040=2.0mm d1041=2.0mm d1042=45.0deg d1043=2.0mm d1044=2.0mm d1045=45.0deg d1046=17.0mm d1047=31.0mm d1048=31.0mm d1049=22.0mm d1050=17.0mm d1051=2.0mm d1052=0.0mm d1053=1.0mm d1054=23.0mm d1055=12.0mm d1056=12.0mm d1057=12.0mm d1058=1.0mm d1059=1.0mm d1060=10.0mm d1061=0.0mm d1062=2.0mm d1063=10.0mm d1064=0.0mm d1065=4.0mm d1066=15.0mm d1067=2.7mm d1068=2.7mm d1069=1.5mm d1070=5.0mm d1071=5.0mm d1072=2.0mm d1073=10.0mm d1074=10.0mm d1075=0.05mm d1076=0.05mm d1077=25.9mm d1078=25.9mm d1079=0.5mm d1080=0.5mm d1081=0.5mm d1082=0.5mm d1083=0.5mm d1084=0.5mm d1085=0.5mm d1086=0.5mm d1087=0.5mm d1088=0.5mm d1089=0.2mm d1090=0.2mm d1091=0.2mm d1092=0.2mm d1093=0.0mm d1094=0.0mm d1095=2.0mm d1096=2.0mm d1097=45.0deg]
  projected_geometry  "Projected Loop120"
  projected_geometry  "Projected Loop121"
  projected_geometry  "Projected Loop122"
  projected_geometry  "Projected Loop123"
  projected_geometry  "Projected Loop124"
  other  "sqr-connector:1"
  other  "sqr-connector:2"
note: 9 required parameter values undecoded (feature->parameter linkage not recoverable at this tier; creation-order binding heuristic only, values carry confidence <= 0.55)
